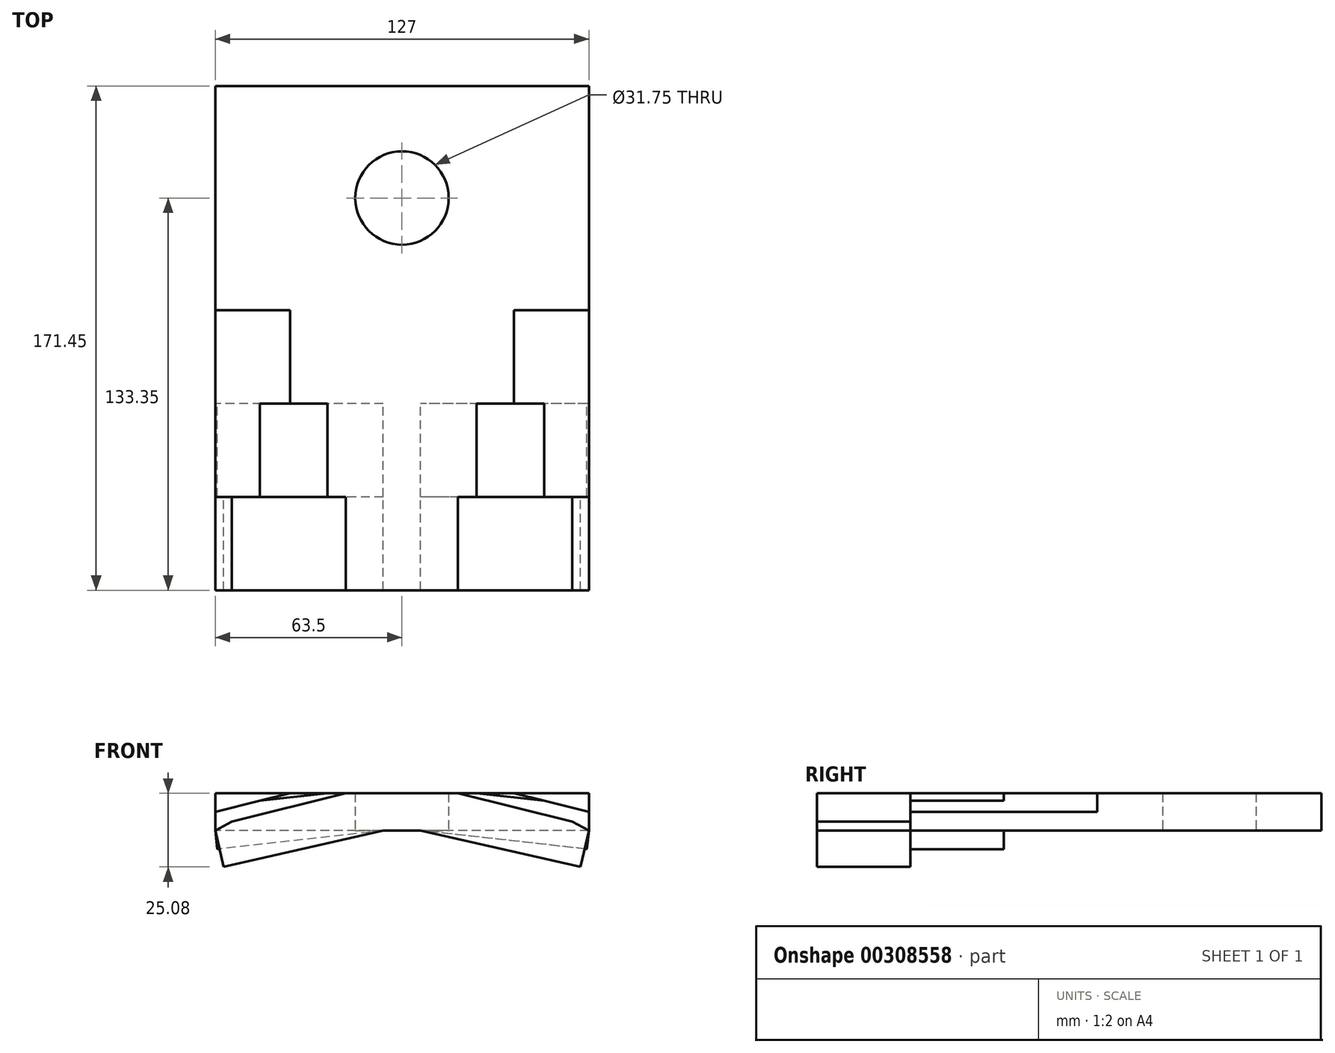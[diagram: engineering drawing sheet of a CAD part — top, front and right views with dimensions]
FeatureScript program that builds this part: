
annotation { "Feature Type Name" : "Feature", "Feature Type Description" : "" }
export const myFeature = defineFeature(function(context is Context, id is Id, definition is map)
    precondition{}
    {
        {
            var Q0;
            Q0=qCreatedBy(makeId("Top.planeOp"),FACE);
            var sketch = newSketch(context, id + "F0", { "sketchPlane" : qUnion([Q0])});
            skLineSegment(sketch, "E0.bottom", {"start": v(-63.5, 76.2) * mm, "end": v(63.5, 76.2) * mm});
            skLineSegment(sketch, "E0.top", {"start": v(-63.5, 0) * mm, "end": v(63.5, 0) * mm});
            skLineSegment(sketch, "E0.left", {"start": v(-63.5, 76.2) * mm, "end": v(-63.5, 0) * mm});
            skLineSegment(sketch, "E0.right", {"start": v(63.5, 76.2) * mm, "end": v(63.5, 0) * mm});
            skCircle(sketch, "E1", {"center": v(0, 38.1) * mm, "radius": 15.88 * mm});
            skSolve(sketch);
        }
        {
            var Q0;
            Q0 = qSketchRegion(id + "F0", true);
            extrude(context, id + "F1", {"entities" : qUnion([Q0]), "depth" : 12.7 * mm});
        }
        {
            var Q0;
            Q0=qCreatedBy(makeId("Front.planeOp"),FACE);
            var sketch = newSketch(context, id + "F2", { "sketchPlane" : qUnion([Q0])});
            skLineSegment(sketch, "E2", {"start": v(0, 0) * mm, "end": v(-6.35, 0) * mm});
            skLineSegment(sketch, "E3", {"start": v(-6.35, 0) * mm, "end": v(-63.5, 0) * mm});
            skLineSegment(sketch, "E4", {"start": v(-38.1, 12.7) * mm, "end": v(38.1, 12.7) * mm});
            skLineSegment(sketch, "E5", {"start": v(63.5, 0) * mm, "end": v(6.35, 0) * mm});
            skLineSegment(sketch, "E6", {"start": v(6.35, 0) * mm, "end": v(0, 0) * mm});
            skLineSegment(sketch, "E7", {"start": v(-63.5, 0) * mm, "end": v(-63.5, 6.35) * mm});
            skLineSegment(sketch, "E8", {"start": v(-63.5, 6.35) * mm, "end": v(-38.1, 12.7) * mm});
            skLineSegment(sketch, "E9", {"start": v(63.5, 0) * mm, "end": v(63.5, 6.35) * mm});
            skLineSegment(sketch, "E10", {"start": v(63.5, 6.35) * mm, "end": v(38.1, 12.7) * mm});
            skSolve(sketch);
        }
        {
            var Q0;
            Q0 = qSketchRegion(id + "F2", true);
            extrude(context, id + "F3", {"entities" : qUnion([Q0]), "operationType" : NewBodyOperationType.ADD, "depth" : 31.75 * mm});
        }
        {
            var Q0;
            Q0=qCreatedBy(makeId("Front.planeOp"),FACE);
            var sketch = newSketch(context, id + "F4", { "sketchPlane" : qUnion([Q0])});
            skLineSegment(sketch, "E11", {"start": v(0, 0) * mm, "end": v(-6.35, 0) * mm});
            skLineSegment(sketch, "E12", {"start": v(-6.35, 0) * mm, "end": v(-62.8, -6.31) * mm});
            skLineSegment(sketch, "E13", {"start": v(-62.8, -6.31) * mm, "end": v(-63.5, 0) * mm});
            skLineSegment(sketch, "E14", {"start": v(-63.5, 0) * mm, "end": v(-63.5, 6.35) * mm});
            skLineSegment(sketch, "E15", {"start": v(-63.5, 6.35) * mm, "end": v(-48.37, 10.13) * mm});
            skLineSegment(sketch, "E16", {"start": v(-48.37, 10.13) * mm, "end": v(-25.4, 12.7) * mm});
            skLineSegment(sketch, "E17", {"start": v(-25.4, 12.7) * mm, "end": v(25.4, 12.7) * mm});
            skLineSegment(sketch, "E18", {"start": v(25.4, 12.7) * mm, "end": v(48.37, 10.13) * mm});
            skLineSegment(sketch, "E19", {"start": v(48.37, 10.13) * mm, "end": v(63.5, 6.35) * mm});
            skLineSegment(sketch, "E20", {"start": v(63.5, 6.35) * mm, "end": v(63.5, 0) * mm});
            skLineSegment(sketch, "E21", {"start": v(63.5, 0) * mm, "end": v(62.8, -6.31) * mm});
            skLineSegment(sketch, "E22", {"start": v(62.8, -6.31) * mm, "end": v(6.35, 0) * mm});
            skLineSegment(sketch, "E23", {"start": v(6.35, 0) * mm, "end": v(0, 0) * mm});
            skSolve(sketch);
        }
        {
            var Q0;
            Q0 = qSketchRegion(id + "F4", true);
            extrude(context, id + "F5", {"entities" : qUnion([Q0]), "operationType" : NewBodyOperationType.ADD, "depth" : 63.5 * mm, "hasSecondDirection" : true, "secondDirectionOppositeDirection" : false, "secondDirectionDepth" : 31.75 * mm});
        }
        {
            var Q0;
            Q0=qCreatedBy(makeId("Front.planeOp"),FACE);
            var sketch = newSketch(context, id + "F6", { "sketchPlane" : qUnion([Q0])});
            skLineSegment(sketch, "E24", {"start": v(0, 0) * mm, "end": v(-6.35, 0) * mm});
            skLineSegment(sketch, "E25", {"start": v(-6.35, 0) * mm, "end": v(-60.68, -12.38) * mm});
            skLineSegment(sketch, "E26", {"start": v(-60.68, -12.38) * mm, "end": v(-63.5, 0) * mm});
            skLineSegment(sketch, "E27", {"start": v(-63.5, 0) * mm, "end": v(-57.8, 3.01) * mm});
            skLineSegment(sketch, "E28", {"start": v(-57.8, 3.01) * mm, "end": v(-19.05, 12.7) * mm});
            skLineSegment(sketch, "E29", {"start": v(-19.05, 12.7) * mm, "end": v(19.05, 12.7) * mm});
            skLineSegment(sketch, "E30", {"start": v(19.05, 12.7) * mm, "end": v(57.8, 3.01) * mm});
            skLineSegment(sketch, "E31", {"start": v(57.8, 3.01) * mm, "end": v(63.5, 0) * mm});
            skLineSegment(sketch, "E32", {"start": v(63.5, 0) * mm, "end": v(60.68, -12.38) * mm});
            skLineSegment(sketch, "E33", {"start": v(60.68, -12.38) * mm, "end": v(6.35, 0) * mm});
            skLineSegment(sketch, "E34", {"start": v(6.35, 0) * mm, "end": v(0, 0) * mm});
            skSolve(sketch);
        }
        {
            var Q0;
            Q0 = qSketchRegion(id + "F6", true);
            extrude(context, id + "F7", {"entities" : qUnion([Q0]), "operationType" : NewBodyOperationType.ADD, "depth" : 95.25 * mm, "hasSecondDirection" : true, "secondDirectionOppositeDirection" : false, "secondDirectionDepth" : 63.5 * mm});
        }
    });
